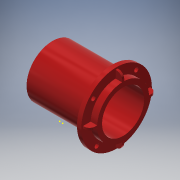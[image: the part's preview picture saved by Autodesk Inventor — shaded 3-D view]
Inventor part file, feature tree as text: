
AUTODESK INVENTOR PART (.ipt)
format: ipt  version: 2019 (Build 230136000, 136)  size: 869,376 bytes
history: native  units: mm
features: sketch x36, extrude x34, projected_geometry x14, fillet x5, other x3
ambient origin geometry x8: Origin, YZ Plane, XZ Plane, XY Plane, X Axis, Y Axis, Z Axis, Center Point
bodies: Body1 (feature_tree), Body2 (feature_tree)
feature tree (92):
  other  "Твердое тело1"
  other  "0ae4c1a17e304db4a8c8e39318f74883.stl"
  extrude  "Выдавливание1"  Depth=3.0mm TaperAngle=0.0deg
  extrude  "Выдавливание2"  Depth=43.0mm
  extrude  "Выдавливание3"  Depth=25.0mm TaperAngle=0.0deg
  extrude  "Выдавливание4"  Depth=20.0mm
  extrude  "Выдавливание5"  Depth=20.0mm
  extrude  "Выдавливание6"  Depth=50.0mm TaperAngle=0.0deg
  extrude  "Выдавливание7"  Depth=34.0mm
  extrude  "Выдавливание8"  Depth=2.0mm
  extrude  "Выдавливание9"  Depth=2.0mm
  extrude  "Выдавливание10"  Depth=1.0mm TaperAngle=0.0deg
  sketch  "Эскиз15"
  sketch  "Эскиз16"
  extrude  "Выдавливание11"  Depth=25.0mm TaperAngle=0.0deg
  extrude  "Выдавливание12"  Depth=4.0mm
  extrude  "Выдавливание13"  Depth=4.0mm
  extrude  "Выдавливание14"  Depth=4.0mm
  extrude  "Выдавливание15"  Depth=4.0mm
  extrude  "Выдавливание16"  Depth=4.5mm
  fillet  "Сопряжение1"  Radius=4.5mm
  fillet  "Сопряжение2"  Radius=4.5mm
  extrude  "Выдавливание17"  Depth=4.5mm
  extrude  "Выдавливание18"  Depth=25.0mm TaperAngle=0.0deg
  extrude  "Выдавливание19"  Depth=7.2mm
  extrude  "Выдавливание20"  Depth=7.2mm
  extrude  "Выдавливание21"  Depth=7.2mm
  extrude  "Выдавливание22"  Depth=7.2mm
  fillet  "Сопряжение3"  Radius=2.0mm
  extrude  "Выдавливание23"  Depth=15.0mm TaperAngle=0.0deg
  extrude  "Выдавливание24"  Depth=15.0mm
  extrude  "Выдавливание25"  Depth=3.0mm
  extrude  "Выдавливание26"  Depth=13.663525mm
  extrude  "Выдавливание27"  Depth=30.32705mm
  extrude  "Выдавливание28"  Depth=8.5mm TaperAngle=0.0deg
  fillet  "Сопряжение4"  Radius=8.5mm
  extrude  "Выдавливание29"  Depth=38.8mm
  extrude  "Выдавливание30"  Depth=22.0mm TaperAngle=0.0deg
  extrude  "Выдавливание31"  Depth=25.0mm TaperAngle=0.0deg
  extrude  "Выдавливание32"  Depth=10.0mm TaperAngle=0.0deg
  fillet  "Сопряжение5"  Radius=3.5mm
  sketch  "Эскиз38"
  extrude  "Выдавливание33"  Depth=3.5mm TaperAngle=0.0deg
  extrude  "Выдавливание34"  Depth=1.0mm TaperAngle=0.0deg
  sketch  "Эскиз2"
  sketch  "Эскиз3"
  sketch  "Эскиз5"
  sketch  "Эскиз6"
  projected_geometry  "Спроецированная петля1"
  sketch  "Эскиз8"
  sketch  "Эскиз9"
  projected_geometry  "Спроецированная петля3"
  sketch  "Эскиз11"
  sketch  "Эскиз12"
  projected_geometry  "Спроецированная петля4"
  sketch  "Эскиз13"
  sketch  "Эскиз14"
  sketch  "Эскиз17"
  sketch  "Эскиз18"
  projected_geometry  "Спроецированная петля5"
  sketch  "Эскиз19"
  projected_geometry  "Спроецированная петля6"
  projected_geometry  "Спроецированная петля7"
  sketch  "Эскиз20"
  projected_geometry  "Спроецированная петля8"
  sketch  "Эскиз21"
  projected_geometry  "Спроецированная петля9"
  sketch  "Эскиз22"
  projected_geometry  "Спроецированная петля10"
  sketch  "Эскиз23"
  sketch  "Эскиз24"
  sketch  "Эскиз25"
  sketch  "Эскиз26"
  sketch  "Эскиз27"
  sketch  "Эскиз28"
  sketch  "Эскиз29"
  sketch  "Эскиз30"
  sketch  "Эскиз31"
  projected_geometry  "Спроецированная петля11"
  sketch  "Эскиз32"
  projected_geometry  "Спроецированная петля12"
  sketch  "Эскиз33"
  sketch  "Эскиз34"
  sketch  "Эскиз35"
  projected_geometry  "Спроецированная петля13"
  sketch  "Эскиз36"
  sketch  "Эскиз37"
  sketch  "Эскиз39"
  projected_geometry  "Спроецированная петля14"
  sketch  "Эскиз40"
  projected_geometry  "Спроецированная петля15"
  other  "ЭлементСетки1"
